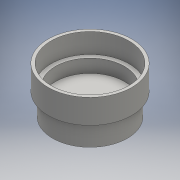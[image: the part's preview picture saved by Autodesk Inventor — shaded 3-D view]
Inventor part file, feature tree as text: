
AUTODESK INVENTOR PART (.ipt)
format: ipt  version: 2016 (Build 200138000, 138)  size: 128,000 bytes
history: native  units: mm
features: extrude x5, sketch x5
ambient origin geometry x8: Origin, YZ Plane, XZ Plane, XY Plane, X Axis, Y Axis, Z Axis, Center Point
bodies: Solid1 (feature_tree)
feature tree (10):
  extrude  "Extrusion1"  Depth=15.0mm TaperAngle=0.0deg
  extrude  "Extrusion2"  Depth=16.5mm TaperAngle=0.0deg
  extrude  "Extrusion3"  Depth=13.5mm TaperAngle=0.0deg
  extrude  "Extrusion4"  Depth=9.0mm TaperAngle=0.0deg
  extrude  "Extrusion5"  Depth=9.0mm TaperAngle=0.0deg
  sketch  "Sketch1"  dims[d0=50.8mm d1=15.0mm d2=0.0mm]
  sketch  "Sketch2"  dims[d3=56.8mm d4=16.5mm d5=0.0mm]
  sketch  "Sketch3"  dims[d6=52.8mm d7=13.5mm d8=0.0mm]
  sketch  "Sketch4"  dims[d9=46.8mm d10=9.0mm d11=0.0mm]
  sketch  "Sketch5"  dims[d12=10.0mm d13=9.0mm d14=0.0mm]
